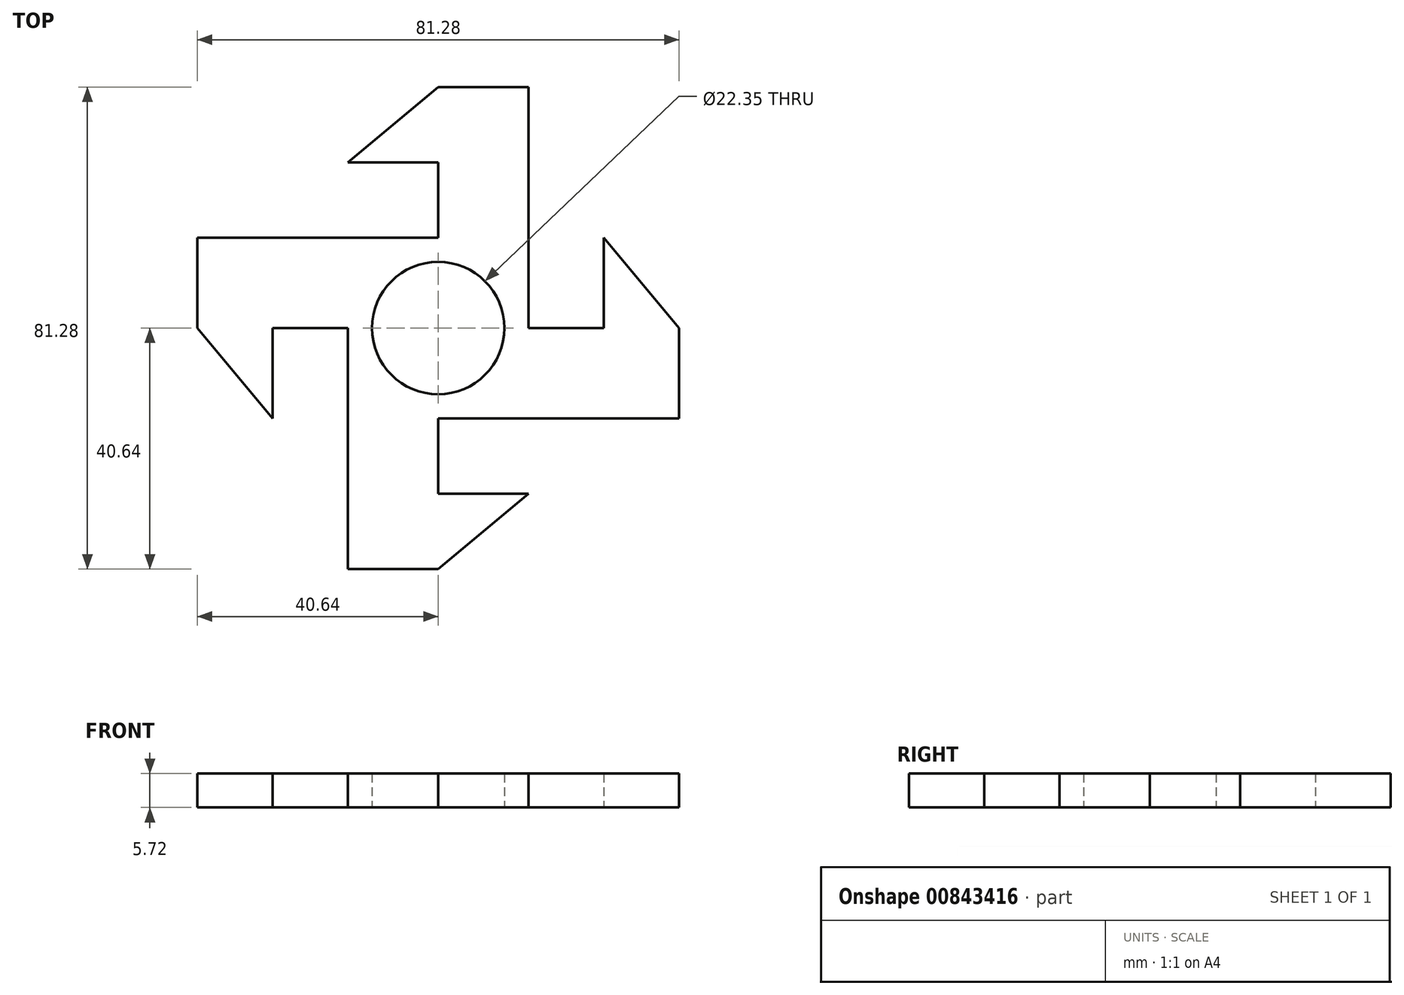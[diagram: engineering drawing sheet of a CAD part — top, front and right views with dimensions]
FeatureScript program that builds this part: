
annotation { "Feature Type Name" : "Feature", "Feature Type Description" : "" }
export const myFeature = defineFeature(function(context is Context, id is Id, definition is map)
    precondition{}
    {
        {
            var Q0;
            Q0=qCreatedBy(makeId("Top.planeOp"),FACE);
            var sketch = newSketch(context, id + "F0", { "sketchPlane" : qUnion([Q0])});
            skCircle(sketch, "E0", {"center": v(0, 0) * mm, "radius": 15.24 * mm});
            skLineSegment(sketch, "E1", {"start": v(0, 15.24) * mm, "end": v(0, 40.64) * mm});
            skLineSegment(sketch, "E2", {"start": v(15.24, 0) * mm, "end": v(40.64, 0) * mm});
            skLineSegment(sketch, "E3", {"start": v(0, -15.24) * mm, "end": v(0, -40.64) * mm});
            skLineSegment(sketch, "E4", {"start": v(-40.64, 0) * mm, "end": v(-15.24, 0) * mm});
            skLineSegment(sketch, "E5", {"start": v(-15.24, -40.64) * mm, "end": v(-15.24, 0) * mm});
            skLineSegment(sketch, "E6", {"start": v(0, -15.24) * mm, "end": v(40.64, -15.24) * mm});
            skLineSegment(sketch, "E7", {"start": v(15.24, 0) * mm, "end": v(15.24, 40.64) * mm});
            skLineSegment(sketch, "E8", {"start": v(0, 15.24) * mm, "end": v(-40.64, 15.24) * mm});
            skLineSegment(sketch, "E9", {"start": v(-40.64, 15.24) * mm, "end": v(-40.64, 0) * mm});
            skLineSegment(sketch, "E10", {"start": v(-15.24, -40.64) * mm, "end": v(0, -40.64) * mm});
            skLineSegment(sketch, "E11", {"start": v(40.64, -15.24) * mm, "end": v(40.64, 0) * mm});
            skLineSegment(sketch, "E12", {"start": v(15.24, 40.64) * mm, "end": v(0, 40.64) * mm});
            skCircle(sketch, "E13", {"center": v(0, 0) * mm, "radius": 11.18 * mm});
            skPoint(sketch, "E14.start.orphan", {"position": v(20.32, -20.32) * mm});
            skLineSegment(sketch, "E15", {"start": v(0, -40.64) * mm, "end": v(15.24, -27.94) * mm});
            skPoint(sketch, "E15.endSnap0", {"position": v(0, -27.94) * mm});
            skLineSegment(sketch, "E16", {"start": v(15.24, -27.94) * mm, "end": v(0, -27.94) * mm});
            skPoint(sketch, "E17.end.orphan", {"position": v(20.32, 0) * mm});
            skPoint(sketch, "E17.start.orphan", {"position": v(20.32, 20.32) * mm});
            skLineSegment(sketch, "E18", {"start": v(40.64, 0) * mm, "end": v(27.94, 15.24) * mm});
            skPoint(sketch, "E18.endSnap0", {"position": v(27.94, 0) * mm});
            skLineSegment(sketch, "E19", {"start": v(27.94, 15.24) * mm, "end": v(27.94, 0) * mm});
            skPoint(sketch, "E20.end.orphan", {"position": v(0, 20.32) * mm});
            skPoint(sketch, "E20.start.orphan", {"position": v(-20.32, 20.32) * mm});
            skLineSegment(sketch, "E21", {"start": v(0, 40.64) * mm, "end": v(-15.24, 27.94) * mm});
            skPoint(sketch, "E21.endSnap0", {"position": v(0, 27.94) * mm});
            skLineSegment(sketch, "E22", {"start": v(-15.24, 27.94) * mm, "end": v(0, 27.94) * mm});
            skPoint(sketch, "E23.start.orphan", {"position": v(-20.32, -20.32) * mm});
            skLineSegment(sketch, "E24", {"start": v(-40.64, 0) * mm, "end": v(-27.94, -15.24) * mm});
            skPoint(sketch, "E24.endSnap0", {"position": v(-27.94, 0) * mm});
            skLineSegment(sketch, "E25", {"start": v(-27.94, -15.24) * mm, "end": v(-27.94, 0) * mm});
            skSolve(sketch);
        }
        {
            var Q0;
            {var subQ0=sQuery(id+"F0.wireOp",EDGE,"E0");var subQ1=makeQuery(id+"F0.imprint","INTERSECT",VERTEX,{"derivedFrom":[subQ0,sQuery(id+"F0.wireOp",EDGE,"E1"),sQuery(id+"F0.wireOp",EDGE,"E8")]});Q0=makeQuery(id+"F0.imprint","IMPRINT",FACE,{"disambiguationData":[TD([[makeQuery(id+"F0.imprint","IMPRINT",EDGE,{"disambiguationData":[TD([[subQ1,1.0]])],"derivedFrom":subQ0}),1.0]])]});}
            var Q1;
            {var subQ0=sQuery(id+"F0.wireOp",EDGE,"E6");Q1=makeQuery(id+"F0.imprint","IMPRINT",FACE,{"disambiguationData":[TD([[makeQuery(id+"F0.imprint","IMPRINT",EDGE,{"derivedFrom":subQ0}),1.0]])]});}
            var Q2;
            {var subQ0=sQuery(id+"F0.wireOp",EDGE,"10ebjHzi-xiyd-FHM3-veY3-r94kub4h1Lga");Q2=makeQuery(id+"F0.imprint","IMPRINT",FACE,{"disambiguationData":[TD([[makeQuery(id+"F0.imprint","IMPRINT",EDGE,{"derivedFrom":subQ0}),-1.0]])]});}
            var Q3;
            {var subQ0=sQuery(id+"F0.wireOp",EDGE,"E7");Q3=makeQuery(id+"F0.imprint","IMPRINT",FACE,{"disambiguationData":[TD([[makeQuery(id+"F0.imprint","IMPRINT",EDGE,{"derivedFrom":subQ0}),1.0]])]});}
            var Q4;
            {var subQ0=sQuery(id+"F0.wireOp",EDGE,"sNcsmoLV-lIFU-FXYS-F87p-aq2kljkgygFf");Q4=makeQuery(id+"F0.imprint","IMPRINT",FACE,{"disambiguationData":[TD([[makeQuery(id+"F0.imprint","IMPRINT",EDGE,{"derivedFrom":subQ0}),-1.0]])]});}
            var Q5;
            {var subQ0=sQuery(id+"F0.wireOp",EDGE,"E8");Q5=makeQuery(id+"F0.imprint","IMPRINT",FACE,{"disambiguationData":[TD([[makeQuery(id+"F0.imprint","IMPRINT",EDGE,{"derivedFrom":subQ0}),1.0]])]});}
            var Q6;
            {var subQ0=sQuery(id+"F0.wireOp",EDGE,"E23");Q6=makeQuery(id+"F0.imprint","IMPRINT",FACE,{"disambiguationData":[TD([[makeQuery(id+"F0.imprint","IMPRINT",EDGE,{"derivedFrom":subQ0}),-1.0]])]});}
            var Q7;
            {var subQ0=sQuery(id+"F0.wireOp",EDGE,"E5");Q7=makeQuery(id+"F0.imprint","IMPRINT",FACE,{"disambiguationData":[TD([[makeQuery(id+"F0.imprint","IMPRINT",EDGE,{"derivedFrom":subQ0}),-1.0]])]});}
            var Q8;
            {var subQ0=sQuery(id+"F0.wireOp",EDGE,"8IaUCp9v-f198-7Lbf-yl9C-eceaHXAMtxie");Q8=makeQuery(id+"F0.imprint","IMPRINT",FACE,{"disambiguationData":[TD([[makeQuery(id+"F0.imprint","IMPRINT",EDGE,{"derivedFrom":subQ0}),-1.0]])]});}
            extrude(context, id + "F1", {"entities" : qUnion([Q0, Q1, Q2, Q3, Q4, Q5, Q6, Q7, Q8]), "depth" : 5.7 * mm, "offsetDistance" : 25.4 * mm});
        }
        {
            var Q0;
            Q0 = qSketchRegion(id + "F0", true);
            extrude(context, id + "F2", {"entities" : qUnion([Q0]), "operationType" : NewBodyOperationType.ADD, "depth" : 5.7 * mm, "offsetDistance" : 25.4 * mm});
        }
    });
